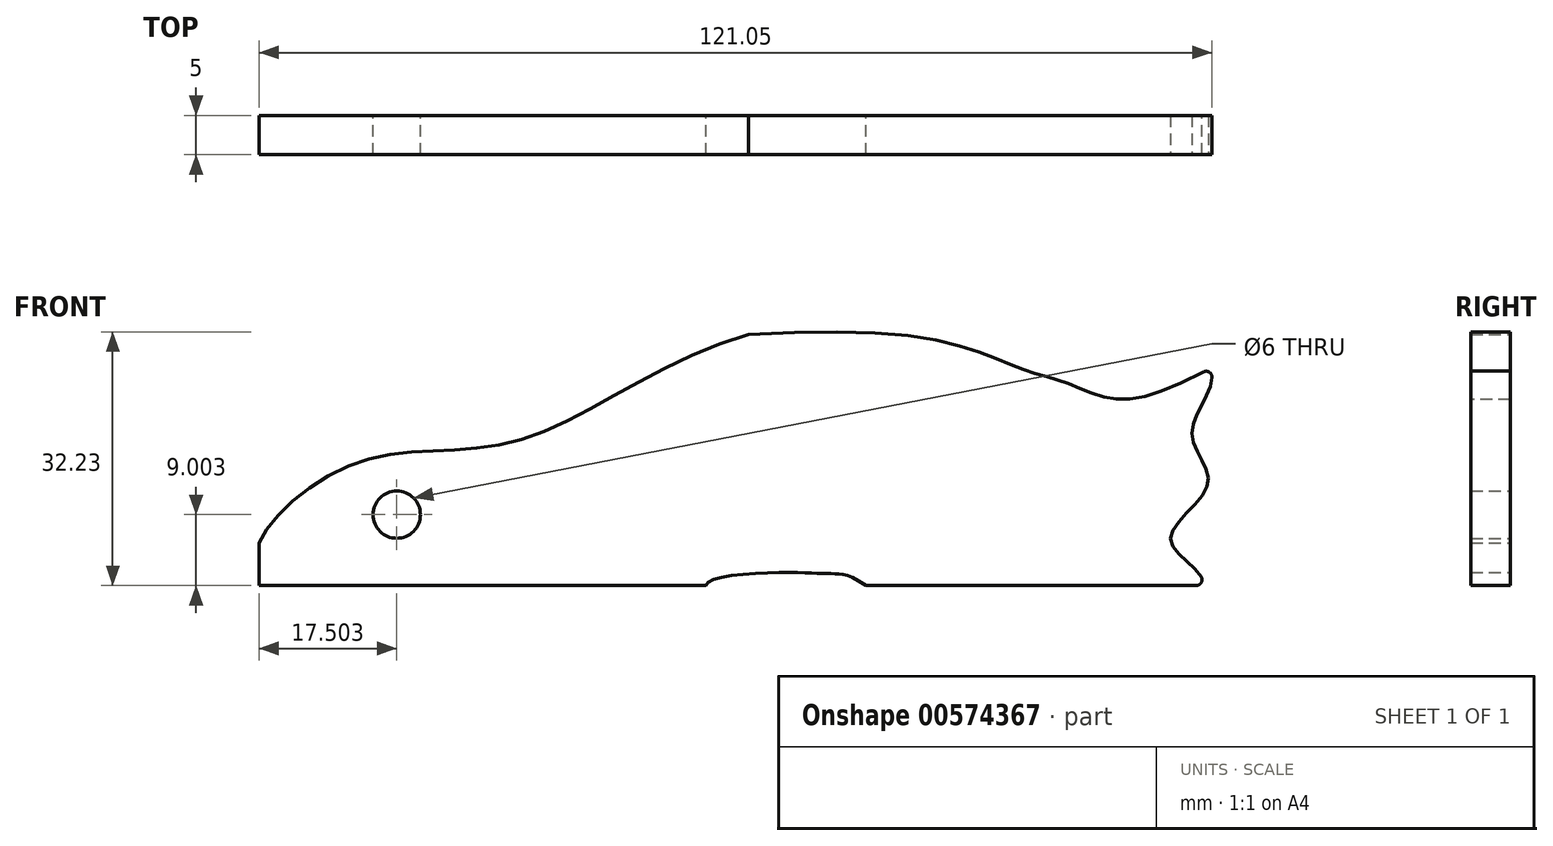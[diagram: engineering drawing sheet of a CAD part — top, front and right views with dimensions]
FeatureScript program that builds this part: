
annotation { "Feature Type Name" : "Feature", "Feature Type Description" : "" }
export const myFeature = defineFeature(function(context is Context, id is Id, definition is map)
    precondition{}
    {
        {
            var Q0;
            Q0=qCreatedBy(makeId("Front.planeOp"),FACE);
            var sketch = newSketch(context, id + "F0", { "sketchPlane" : qUnion([Q0])});
            skLineSegment(sketch, "E0", {"start": v(48.82, 8.27) * mm, "end": v(10.95, 8.27) * mm});
            skLineSegment(sketch, "E1", {"start": v(-64.93, 17.27) * mm, "end": v(53.82, 17.27) * mm, "construction": true});
            skLineSegment(sketch, "E2", {"start": v(-48.68, 20.27) * mm, "end": v(-48.68, 8.27) * mm, "construction": true});
            skLineSegment(sketch, "E3", {"start": v(36.32, 20.27) * mm, "end": v(36.32, 8.27) * mm, "construction": true});
            skPoint(sketch, "E4", {"position": v(-48.68, 19.72) * mm});
            skCircle(sketch, "E5", {"center": v(-48.68, 17.27) * mm, "radius": 3 * mm});
            skCircle(sketch, "E6", {"center": v(36.32, 17.27) * mm, "radius": 3 * mm, "construction": true});
            skPoint(sketch, "E7.visualSharp", {"position": v(-66.18, 8.27) * mm});
            skPoint(sketch, "E8.visualSharp", {"position": v(53.82, 8.27) * mm});
            skPoint(sketch, "E9.orphan", {"position": v(-48.68, 31.17) * mm});
            skPoint(sketch, "E10.end.orphan", {"position": v(-66.18, 43.27) * mm});
            skLineSegment(sketch, "E11", {"start": v(56.54, 43.27) * mm, "end": v(-66.18, 43.27) * mm});
            skLineSegment(sketch, "E12", {"start": v(-66.18, 8.27) * mm, "end": v(-66.18, 43.27) * mm});
            skPoint(sketch, "E13.0.internal.orphan", {"position": v(-66.18, 17.27) * mm});
            skPoint(sketch, "E13.1.internal.orphan", {"position": v(-6.18, 43.27) * mm});
            skPoint(sketch, "E13.startDerivative.orphan", {"position": v(-44.3, 19.72) * mm});
            skPoint(sketch, "E14.endDerivative.orphan", {"position": v(29.35, 33) * mm});
            skPoint(sketch, "E15.end.orphan", {"position": v(50.23, 33) * mm});
            skPoint(sketch, "E16.end.orphan", {"position": v(21.39, 33) * mm});
            skPoint(sketch, "E17.end.orphan", {"position": v(29.35, -16.4) * mm});
            skLineSegment(sketch, "E18", {"start": v(-66.18, 8.27) * mm, "end": v(-51.18, 8.27) * mm});
            skLineSegment(sketch, "E19", {"start": v(48.82, 8.27) * mm, "end": v(52.86, 8.27) * mm});
            skFitSpline(sketch, "E20", {"points": [v(-66.18, 34.77) * mm, v(13.78, 40.26) * mm, v(30.83, 35.72) * mm, v(36.1, 34.11) * mm, v(41.95, 32.04) * mm, v(53.82, 35.43) * mm], "startDerivative": vector(125.26, 2.25) * mm, "endDerivative": vector(103.56, 54.68) * mm});
            skFitSpline(sketch, "E21", {"points": [v(-3.99, 40.15) * mm, v(-33.4, 26.65) * mm, v(-53.38, 24.02) * mm, v(-66.18, 13.7) * mm, v(-66.18, 8.27) * mm], "startDerivative": vector(-101.94, -28.4) * mm, "endDerivative": vector(9.7, -37) * mm});
            skPoint(sketch, "E22.visualSharp", {"position": v(3.98, 29.53) * mm});
            skPoint(sketch, "E23.newPointB", {"position": v(53.82, 43.27) * mm});
            skArc(sketch, "E23.filletArc", {"start": v(54.87, 34.72) * mm, "mid": v(54.53, 35.38) * mm, "end": v(53.78, 35.4) * mm});
            skPoint(sketch, "E24.orphan", {"position": v(53.82, 25.77) * mm});
            skFitSpline(sketch, "E25", {"points": [v(54.87, 34.72) * mm, v(52.34, 27.47) * mm, v(54.33, 21.11) * mm, v(49.62, 14.08) * mm, v(53.82, 8.27) * mm], "startDerivative": vector(-1.05, -26.44) * mm, "endDerivative": vector(-1.05, -26.44) * mm});
            skArc(sketch, "E26.filletArc", {"start": v(52.86, 8.27) * mm, "mid": v(53.51, 8.65) * mm, "end": v(53.51, 9.4) * mm});
            skPoint(sketch, "E27.trimOffspring.2.internal.orphan", {"position": v(0, 24.08) * mm});
            skPoint(sketch, "E28.2.internal.orphan", {"position": v(8.03, 22.4) * mm});
            skPoint(sketch, "E28.endDerivative.orphan", {"position": v(0, 22.45) * mm});
            skPoint(sketch, "E28.startDerivative.orphan", {"position": v(-15.02, 22.4) * mm});
            skFitSpline(sketch, "E29", {"points": [v(-9.37, 8.27) * mm, v(0, 9.93) * mm, v(5.5, 9.8) * mm, v(7.41, 9.75) * mm, v(10.95, 8.27) * mm], "startDerivative": vector(-0.57, 10.58) * mm, "endDerivative": vector(24.1, -16.48) * mm});
            skLineSegment(sketch, "E30.trimOffspring", {"start": v(-9.37, 8.27) * mm, "end": v(-51.18, 8.27) * mm});
            skSolve(sketch);
        }
        {
            var Q0;
            Q0=makeQuery(id+"F0.imprint","IMPRINT",FACE,{"disambiguationData":[TD([[makeQuery(id+"F0.imprint","IMPRINT",EDGE,{"derivedFrom":sQuery(id+"F0.wireOp",EDGE,"E0")}),-1.0]])]});
            extrude(context, id + "F1", {"entities" : qUnion([Q0]), "depth" : 5 * mm, "offsetDistance" : 25 * mm});
        }
    });
